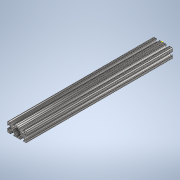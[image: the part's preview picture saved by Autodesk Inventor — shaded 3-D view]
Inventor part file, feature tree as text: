
AUTODESK INVENTOR PART (.ipt)
format: ipt  version: 2020 (Build 240168000, 168)  size: 347,648 bytes
history: native  units: in
note: dims shown in document units (in); Inventor stores cm internally (conversion verified against a paired STEP export)
features: sketch x2, extrude x1
ambient origin geometry x8: Origin, YZ Plane, XZ Plane, XY Plane, X Axis, Y Axis, Z Axis, Center Point
bodies: Solid1 (feature_tree)
feature tree (3):
  extrude  "Extrusion1"  [1 undecoded]
  sketch  "Sketch2"
  sketch  "Sketch1"  dims[d0=15.0in d1=0.0in]
note: 1 required parameter value undecoded (feature->parameter linkage not recoverable at this tier; creation-order binding heuristic only, values carry confidence <= 0.55)
